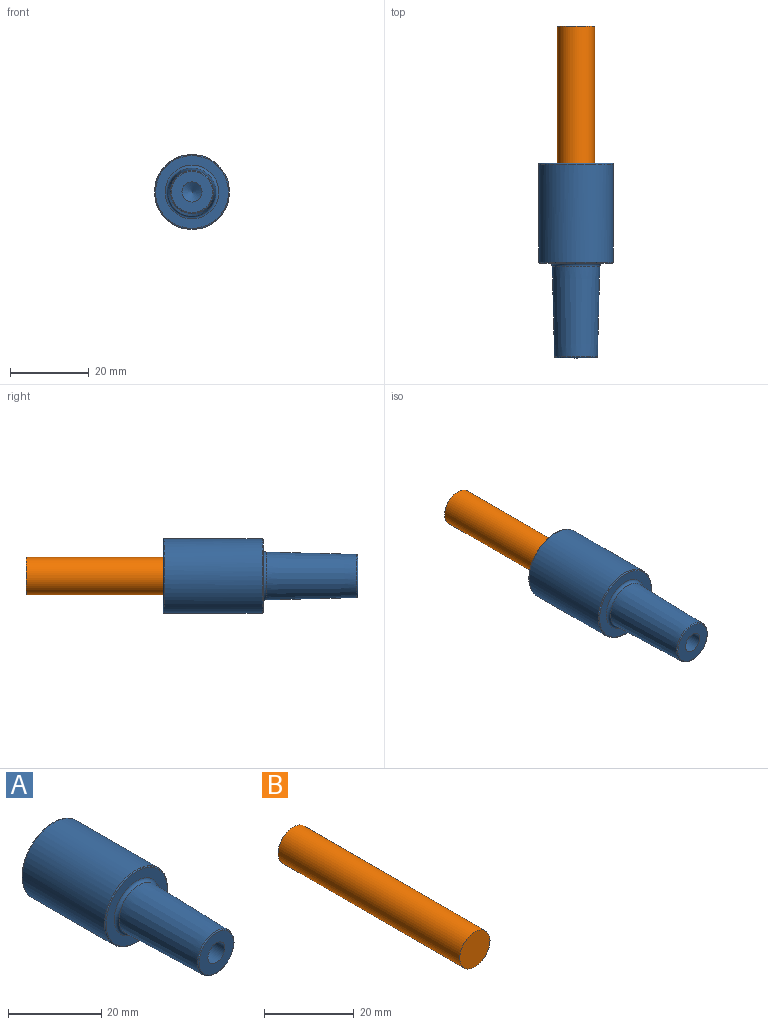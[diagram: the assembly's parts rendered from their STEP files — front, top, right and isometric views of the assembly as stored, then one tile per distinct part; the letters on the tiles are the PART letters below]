
ASSEMBLY  parts=2 mates=1
PART A: 13 faces, bbox 20.6x49.5x20.6 mm
  f0: plane 18.54x18.54mm, normal (0,1,0), area 198.8mm2, adj f8,f11
  f1: cylinder r=9.53mm len=24.89mm, axis (0,-1,0), area 1489.7mm2, adj f8,f9
  f2: plane 18.54x18.54mm, normal (0,-1,0), area 123.1mm2, adj f7,f9
  f3: cone r=6.1mm half-angle=1.4deg, axis (0,1,0), area 841.9mm2, adj f7,f10
  f4: plane 10.49x10.49mm, normal (0,-1,0), area 66mm2, adj f6,f10
  f5: cone r=0mm half-angle=59deg, axis (0,-1,0), area 23.9mm2, adj f6
  f6: cylinder r=2.55mm len=22.23mm, axis (0,-1,0), area 356.5mm2, adj f4,f5
  f7: torus R=6.84mm, axis (0,1,0), area 47.1mm2, adj f2,f3
  f8: torus R=9.27mm, axis (0,-1,0), area 23.6mm2, adj f0,f1
  f9: torus R=9.27mm, axis (0,1,0), area 23.6mm2, adj f1,f2
  f10: torus R=5.25mm, axis (0,1,0), area 13.3mm2, adj f3,f4
  f11: cylinder r=4.76mm len=22.23mm, axis (0,-1,0), area 665.1mm2, adj f0,f12
  f12: plane 9.53x9.53mm, normal (0,1,0), area 71.3mm2, adj f11
PART B: 3 faces, bbox 9.5x57.2x9.5 mm
  f0: plane 9.53x9.53mm, normal (0,-1,0), area 71.3mm2, adj f2
  f1: plane 9.53x9.53mm, normal (0,1,0), area 71.3mm2, adj f2
  f2: cylinder r=4.76mm len=57.15mm, axis (0,-1,0), area 1710.1mm2, adj f0,f1
PLACE A at identity fixed
PLACE B t=(0,31.75,0)mm
MATE fastened B.f2 <-> A.f11  axis (0,-1,0) through (0,3.17,0)mm
